FCSTD DOCUMENT  (FreeCAD 0.18R14555 (Git shallow))
Label: ArduinoHolder
License: All rights reserved
LicenseURL: http://en.wikipedia.org/wiki/All_rights_reserved
objects: Sketcher::SketchObject×1
note: 1 computed .brp shape members not serialized (recipe doc carries the construction recipe); baked Part::Feature solids carry a one-line shape summary decoded from their .brp

FEATURE [Sketcher::SketchObject] Sketch
  MapMode = 5
  sketch-geometry (32):
    g0: LineSegment StartX=0 StartY=0 StartZ=0 EndX=7.5 EndY=0 EndZ=0
    g1: LineSegment StartX=7.5 StartY=0 StartZ=0 EndX=7.5 EndY=2.5 EndZ=0
    g2: LineSegment StartX=7.5 StartY=2.5 StartZ=0 EndX=0 EndY=2.5 EndZ=0
    g3: LineSegment StartX=0 StartY=2.5 StartZ=0 EndX=0 EndY=0 EndZ=0
    g4: LineSegment StartX=7.5 StartY=0 StartZ=0 EndX=15.25 EndY=1e-16 EndZ=0
    g5: LineSegment StartX=15.25 StartY=1e-16 StartZ=0 EndX=15.25 EndY=-2 EndZ=0
    g6: LineSegment [constr] StartX=15.25 StartY=-2 StartZ=0 EndX=-7.75 EndY=-2 EndZ=0
    g7: LineSegment StartX=-7.75 StartY=-2 StartZ=0 EndX=-7.75 EndY=0 EndZ=0
    g8: LineSegment StartX=0 StartY=0 StartZ=0 EndX=-7.75 EndY=0 EndZ=0
    g9: LineSegment StartX=18.25 StartY=-6 StartZ=0 EndX=18.25 EndY=16 EndZ=0
    g10: LineSegment StartX=-10.75 StartY=16 StartZ=0 EndX=18.25 EndY=16 EndZ=0
    g11: LineSegment StartX=-10.75 StartY=16 StartZ=0 EndX=-10.75 EndY=-6 EndZ=0
    g12: LineSegment StartX=-10.75 StartY=-6 StartZ=0 EndX=18.25 EndY=-6 EndZ=0
    g13: LineSegment StartX=-7.75 StartY=-2 StartZ=0 EndX=2.25 EndY=-2 EndZ=0
    g14: LineSegment StartX=5.25 StartY=-2 StartZ=0 EndX=15.25 EndY=-2 EndZ=0
    g15: LineSegment StartX=2.25 StartY=-2 StartZ=0 EndX=2.25 EndY=-3 EndZ=0
    g16: LineSegment StartX=2.25 StartY=-3 StartZ=0 EndX=5.25 EndY=-3 EndZ=0
    g17: LineSegment StartX=5.25 StartY=-2 StartZ=0 EndX=5.25 EndY=-3 EndZ=0
    g18: LineSegment [constr] StartX=5.25 StartY=-3 StartZ=0 EndX=5.25 EndY=-6 EndZ=0
    g19: LineSegment [constr] StartX=15.25 StartY=-2 StartZ=0 EndX=18.25 EndY=-2 EndZ=0
    g20: LineSegment [constr] StartX=-7.75 StartY=-2 StartZ=0 EndX=-10.75 EndY=-2 EndZ=0
    g21: LineSegment StartX=0.75 StartY=7 StartZ=0 EndX=6.75 EndY=7 EndZ=0
    g22: LineSegment StartX=6.75 StartY=7 StartZ=0 EndX=6.75 EndY=13 EndZ=0
    g23: LineSegment StartX=6.75 StartY=13 StartZ=0 EndX=0.75 EndY=13 EndZ=0
    g24: LineSegment StartX=0.75 StartY=13 StartZ=0 EndX=0.75 EndY=7 EndZ=0
    g25: Circle CenterX=3.75 CenterY=10 CenterZ=0 NormalX=0 NormalY=0 NormalZ=1 AngleXU=0 Radius=2
    g26: LineSegment [constr] StartX=3.75 StartY=10 StartZ=0 EndX=6.75 EndY=13 EndZ=0
    g27: LineSegment [constr] StartX=0.75 StartY=13 StartZ=0 EndX=3.75 EndY=10 EndZ=0
    g28: LineSegment [constr] StartX=3.75 StartY=10 StartZ=0 EndX=0.75 EndY=7 EndZ=0
    g29: LineSegment [constr] StartX=0.75 StartY=7 StartZ=0 EndX=0.75 EndY=-6 EndZ=0
    g30: LineSegment [constr] StartX=6.75 StartY=7 StartZ=0 EndX=18.25 EndY=7 EndZ=0
    g31: LineSegment [constr] StartX=0.75 StartY=7 StartZ=0 EndX=-10.75 EndY=7 EndZ=0
  constraints (90):
    c: Coincident(g0,g3)
    c: Coincident(g0,g-1)
    c: Coincident(g0,g1)
    c: Coincident(g7,g8)
    c: Coincident(g6,g7)
    c: Coincident(g5,g6)
    c: Coincident(g4,g5)
    c: Horizontal(g2)
    c: Horizontal(g8)
    c: Horizontal(g6)
    c: Vertical(g1)
    c: Vertical(g3)
    c: Vertical(g7)
    c: Vertical(g5)
    c: Equal(g3,g1)
    c: Equal(g7,g5)
    c: Equal(g8,g4)
    c: DistanceX(g0,g0) = 7.5
    c: DistanceY(g7,g7) = 2
    c: DistanceY(g1,g1) = 2.5
    c: Coincident(g10,g11)
    c: Coincident(g9,g10)
    c: Coincident(g11,g12)
    c: Coincident(g9,g12)
    c: Horizontal(g10)
    c: Horizontal(g12)
    c: Vertical(g11)
    c: Vertical(g9)
    c: DistanceY(g11,g11) = 22
    c: Coincident(g1,g2)
    c: Coincident(g2,g3)
    c: DistanceX(g6,g6) = 23
    c: Coincident(g0,g8)
    c: Coincident(g4,g0)
    c: Coincident(g5,g14)
    c: Coincident(g6,g13)
    c: Horizontal(g13)
    c: Equal(g13,g14)
    c: Coincident(g14,g17)
    c: Coincident(g16,g17)
    c: Coincident(g15,g16)
    c: Coincident(g13,g15)
    c: Vertical(g15)
    c: Vertical(g17)
    c: Horizontal(g16)
    c: DistanceY(g15,g15) = 1
    c: Coincident(g16,g18)
    c: Coincident(g5,g19)
    c: Horizontal(g19)
    c: PointOnObject(g19,g9)
    c: PointOnObject(g18,g12)
    c: DistanceY(g18,g18) = 3
    c: Vertical(g18)
    c: DistanceX(g19,g19) = 3
    c: Coincident(g6,g20)
    c: PointOnObject(g20,g11)
    c: Horizontal(g20)
    c: Equal(g20,g19)
    c: Horizontal(g14)
    c: DistanceX(g16,g16) = 3
    c: Coincident(g21,g22)
    c: Coincident(g22,g23)
    c: Coincident(g23,g24)
    c: Coincident(g24,g21)
    c: Horizontal(g21)
    c: Horizontal(g23)
    c: Vertical(g22)
    c: Vertical(g24)
    c: DistanceX(g23,g23) = 6
    c: DistanceY(g24,g24) = 6
    c: Radius(g25) = 2
    c: Coincident(g25,g26)
    c: Coincident(g25,g27)
    c: Coincident(g23,g27)
    c: Coincident(g22,g26)
    c: Equal(g26,g27)
    c: Coincident(g21,g28)
    c: Coincident(g25,g28)
    c: Equal(g27,g28)
    c: Vertical(g29)
    c: Coincident(g21,g29)
    c: PointOnObject(g29,g12)
    c: DistanceY(g29,g29) = 13
    c: Horizontal(g30)
    c: Horizontal(g31)
    c: PointOnObject(g31,g11)
    c: PointOnObject(g30,g9)
    c: Equal(g30,g31)
    c: Coincident(g21,g30)
    c: Coincident(g21,g31)
